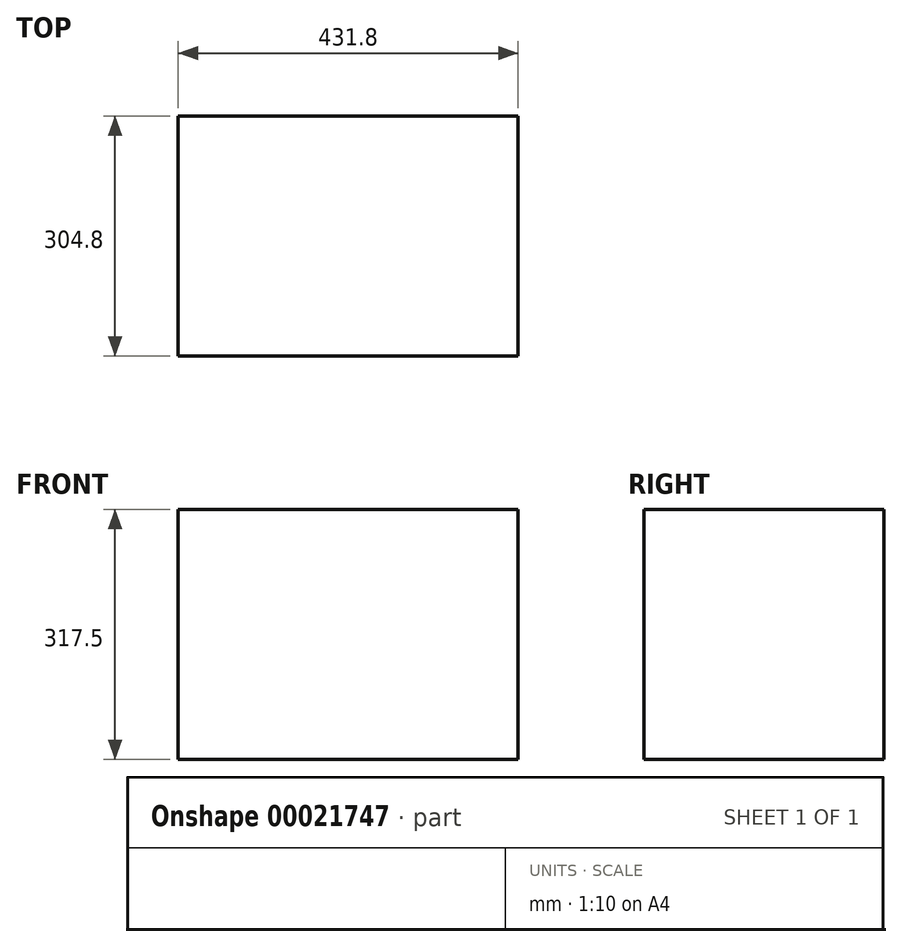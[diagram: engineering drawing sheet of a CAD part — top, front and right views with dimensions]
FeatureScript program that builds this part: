
annotation { "Feature Type Name" : "Feature", "Feature Type Description" : "" }
export const myFeature = defineFeature(function(context is Context, id is Id, definition is map)
    precondition{}
    {
        {
            var Q0;
            Q0=qCreatedBy(makeId("Top.planeOp"),FACE);
            var sketch = newSketch(context, id + "F0", { "sketchPlane" : qUnion([Q0])});
            skLineSegment(sketch, "E0.bottom", {"start": v(215.9, -152.4) * mm, "end": v(-215.9, -152.4) * mm});
            skLineSegment(sketch, "E0.top", {"start": v(215.9, 152.4) * mm, "end": v(-215.9, 152.4) * mm});
            skLineSegment(sketch, "E0.left", {"start": v(215.9, -152.4) * mm, "end": v(215.9, 152.4) * mm});
            skLineSegment(sketch, "E0.right", {"start": v(-215.9, -152.4) * mm, "end": v(-215.9, 152.4) * mm});
            skPoint(sketch, "E0.middle", {"position": v(0, 0) * mm});
            skSolve(sketch);
        }
        {
            var Q0;
            Q0 = qSketchRegion(id + "F0", true);
            extrude(context, id + "F1", {"entities" : qUnion([Q0]), "depth" : 317.5 * mm});
        }
        {
            var Q0;
            Q0=makeQuery(id+"F1.opExtrude","CAP_FACE",FACE,{"disambiguationData":[OSD([sQuery(id+"F0.wireOp",EDGE,"E0.bottom"),sQuery(id+"F0.wireOp",EDGE,"E0.top"),sQuery(id+"F0.wireOp",EDGE,"E0.left"),sQuery(id+"F0.wireOp",EDGE,"E0.right")])],"isStart":false});
            var sketch = newSketch(context, id + "F2", { "sketchPlane" : qUnion([Q0])});
            skLineSegment(sketch, "E1", {"start": v(-215.9, 127) * mm, "end": v(-279.4, 127) * mm});
            skSolve(sketch);
        }
        {
            var Q0;
            Q0=makeQuery(id+"F1.opExtrude","SWEPT_FACE",FACE,{"disambiguationData":[OSD([sQuery(id+"F0.wireOp",EDGE,"E0.top")])]});
            cPlane(context, id + "F3", {"entities" : qUnion([Q0]), "cplaneType" : CPlaneType.OFFSET, "offset" : 25.4 * mm, "oppositeDirection" : true, "width" : 152.4 * mm, "height" : 152.4 * mm});
        }
        {
            var Q0;
            Q0=qCreatedBy(id+"F3.planeOp",FACE);
            var sketch = newSketch(context, id + "F4", { "sketchPlane" : qUnion([Q0])});
            skLineSegment(sketch, "E2", {"start": v(279.4, 317.5) * mm, "end": v(279.4, 381) * mm});
            skSolve(sketch);
        }
        {
            var Q0;
            {var subQ1=makeQuery(id+"F1.opExtrude","CAP_EDGE",EDGE,{"disambiguationData":[OSD([sQuery(id+"F0.wireOp",EDGE,"E0.bottom")])],"isStart":false});Q0=makeQuery(id+"F2.imprint","IMPRINT",FACE,{"disambiguationData":[TD([[makeQuery(id+"F2.imprint","IMPRINT",EDGE,{"derivedFrom":subQ1}),-1.0]])]});}
            cPlane(context, id + "F5", {"entities" : qUnion([Q0]), "cplaneType" : CPlaneType.OFFSET, "offset" : 63.5 * mm, "width" : 152.4 * mm, "height" : 152.4 * mm});
        }
    });
